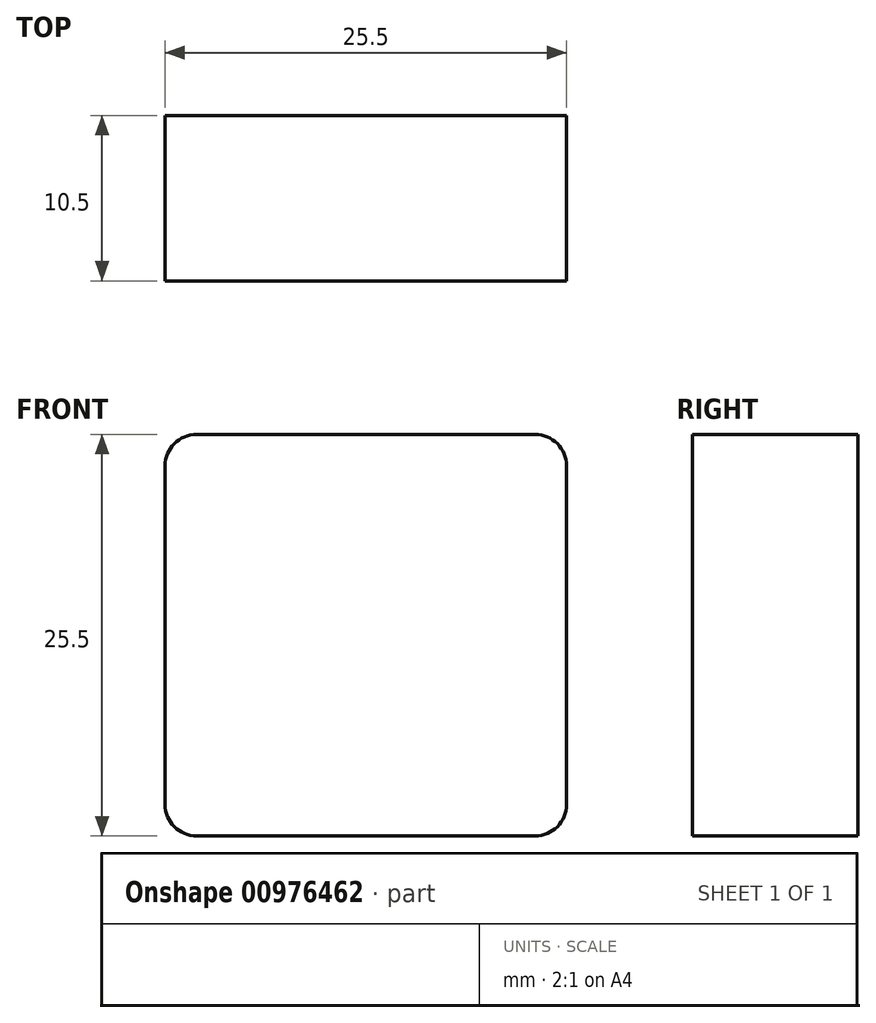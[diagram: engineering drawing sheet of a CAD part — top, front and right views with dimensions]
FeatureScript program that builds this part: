
annotation { "Feature Type Name" : "Feature", "Feature Type Description" : "" }
export const myFeature = defineFeature(function(context is Context, id is Id, definition is map)
    precondition{}
    {
        {
            var Q0;
            Q0=qCreatedBy(makeId("Front.planeOp"),FACE);
            var sketch = newSketch(context, id + "F0", { "sketchPlane" : qUnion([Q0])});
            skLineSegment(sketch, "E0.rect.bottom", {"start": v(12.75, -12.75) * mm, "end": v(-12.75, -12.75) * mm});
            skLineSegment(sketch, "E0.rect.top", {"start": v(12.75, 12.75) * mm, "end": v(-12.75, 12.75) * mm});
            skLineSegment(sketch, "E0.rect.left", {"start": v(12.75, -12.75) * mm, "end": v(12.75, 12.75) * mm});
            skLineSegment(sketch, "E0.rect.right", {"start": v(-12.75, -12.75) * mm, "end": v(-12.75, 12.75) * mm});
            skPoint(sketch, "E0.rect.middle", {"position": v(0, 0) * mm});
            skSolve(sketch);
        }
        {
            var Q0;
            Q0=qSketchRegion(id+"F0",true);
            extrude(context, id + "F1", {"entities" : qUnion([Q0]), "depth" : 10.5 * mm});
        }
        {
            var Q0;
            Q0=makeQuery(id+"F1.opExtrude","SWEPT_EDGE",EDGE,{"disambiguationData":[OSD([sQuery(id+"F0.wireOp",EDGE,"E0.rect.top"),sQuery(id+"F0.wireOp",EDGE,"E0.rect.left")])]});
            var Q1;
            Q1=makeQuery(id+"F1.opExtrude","SWEPT_EDGE",EDGE,{"disambiguationData":[OSD([sQuery(id+"F0.wireOp",EDGE,"E0.rect.bottom"),sQuery(id+"F0.wireOp",EDGE,"E0.rect.left")])]});
            var Q2;
            Q2=makeQuery(id+"F1.opExtrude","SWEPT_EDGE",EDGE,{"disambiguationData":[OSD([sQuery(id+"F0.wireOp",EDGE,"E0.rect.top"),sQuery(id+"F0.wireOp",EDGE,"E0.rect.right")])]});
            var Q3;
            Q3=makeQuery(id+"F1.opExtrude","SWEPT_EDGE",EDGE,{"disambiguationData":[OSD([sQuery(id+"F0.wireOp",EDGE,"E0.rect.bottom"),sQuery(id+"F0.wireOp",EDGE,"E0.rect.right")])]});
            fillet(context, id + "F2", {"entities" : qUnion([Q0, Q1, Q2, Q3]), "radius" : 2 * mm, "tangentPropagation" : true, "allowEdgeOverflow" : false});
        }
    });
